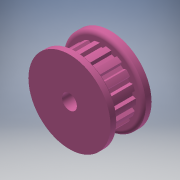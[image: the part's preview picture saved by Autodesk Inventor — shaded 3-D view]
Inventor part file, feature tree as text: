
AUTODESK INVENTOR PART (.ipt)
format: ipt  version: 2017 SP1 (Build 210196100, 196)  size: 258,560 bytes
history: native  units: in
note: dims shown in document units (in); Inventor stores cm internally (conversion verified against a paired STEP export)
features: extrude x4, sketch x4, projected_geometry x1, pattern_circular x1
ambient origin geometry x8: Origin, YZ Plane, XZ Plane, XY Plane, X Axis, Y Axis, Z Axis, Center Point
bodies: Solid1 (feature_tree)
feature tree (10):
  extrude  "Extrusion1"  Depth=1.0in
  extrude  "Extrusion2"  Depth=1.0in TaperAngle=0.0deg
  extrude  "Extrusion3"  [1 undecoded]
  extrude  "Extrusion4"  [1 undecoded]
  sketch  "Sketch1"  dims[d0=1.0in d1=0.0in d2=0.5in]
  projected_geometry  "Projected Loop1"
  sketch  "Sketch2"  dims[d3=1.0in d4=0.0in d5=0.0625in d6=0.0in]
  sketch  "Sketch3"  dims[d7=0.0625in d8=0.0in]
  sketch  "Sketch4"
  pattern_circular  "CirPattern2"
note: 2 required parameter values undecoded (feature->parameter linkage not recoverable at this tier; creation-order binding heuristic only, values carry confidence <= 0.55)
